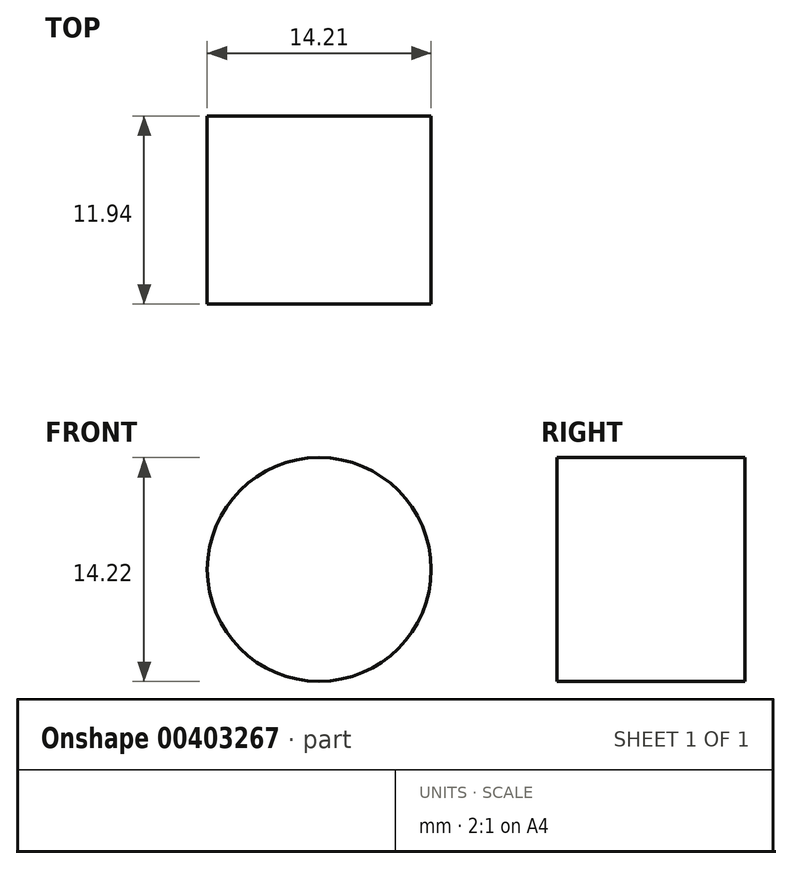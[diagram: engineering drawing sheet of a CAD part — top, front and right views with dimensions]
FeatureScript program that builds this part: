
annotation { "Feature Type Name" : "Feature", "Feature Type Description" : "" }
export const myFeature = defineFeature(function(context is Context, id is Id, definition is map)
    precondition{}
    {
        {
            var Q0;
            Q0=qCreatedBy(makeId("Front.planeOp"),FACE);
            var sketch = newSketch(context, id + "F0", { "sketchPlane" : qUnion([Q0])});
            skCircle(sketch, "E0", {"center": v(-66.34, 47.77) * mm, "radius": 7.1 * mm});
            skSolve(sketch);
        }
        {
            var Q0;
            Q0=makeQuery(id+"F0.imprint","IMPRINT",FACE,{"disambiguationData":[TD([[makeQuery(id+"F0.imprint","IMPRINT",EDGE,{"derivedFrom":sQuery(id+"F0.wireOp",EDGE,"E0")}),1.0]])]});
            extrude(context, id + "F1", {"entities" : qUnion([Q0]), "depth" : 11.94 * mm});
        }
        {
            var Q0;
            Q0=qCreatedBy(makeId("Right.planeOp"),FACE);
            var sketch = newSketch(context, id + "F2", { "sketchPlane" : qUnion([Q0])});
            skFitSpline(sketch, "E1", {"points": [v(-37.13, 35.95) * mm, v(-60.71, 45.13) * mm, v(-28.1, 12.31) * mm, v(-46.67, 0) * mm, v(-63.22, 23.79) * mm], "startDerivative": vector(-165.55, 75) * mm, "endDerivative": vector(-46.37, 134.57) * mm});
            skSolve(sketch);
        }
        {
            var Q0;
            Q0=sQuery(id+"F2.wireOp",EDGE,"E1");
            extrude(context, id + "F3", {"bodyType" : ToolBodyType.SURFACE, "surfaceEntities" : qUnion([Q0]), "depth" : 6.35 * mm});
        }
    });
